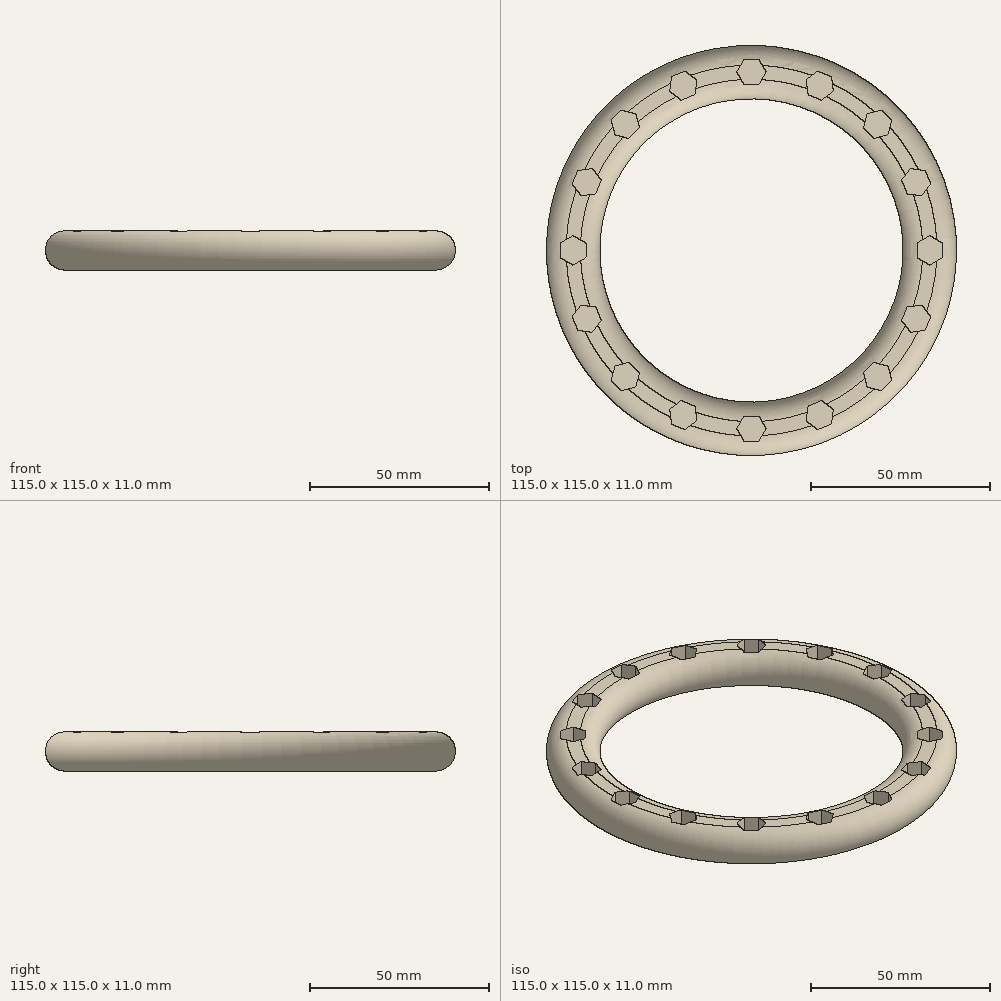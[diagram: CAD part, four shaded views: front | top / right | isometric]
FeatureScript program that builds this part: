
annotation { "Feature Type Name" : "Feature", "Feature Type Description" : "" }
export const myFeature = defineFeature(function(context is Context, id is Id, definition is map)
    precondition{}
    {
        {
            var Q0;
            Q0=qCreatedBy(makeId("Front.planeOp"),FACE);
            var sketch = newSketch(context, id + "F0", { "sketchPlane" : qUnion([Q0])});
            skLineSegment(sketch, "E0.bottom", {"start": v(42.5, 11) * mm, "end": v(57.5, 11) * mm});
            skLineSegment(sketch, "E0.top", {"start": v(42.5, 0) * mm, "end": v(57.5, 0) * mm});
            skLineSegment(sketch, "E0.left", {"start": v(42.5, 11) * mm, "end": v(42.5, 0) * mm});
            skLineSegment(sketch, "E0.right", {"start": v(57.5, 11) * mm, "end": v(57.5, 0) * mm});
            skLineSegment(sketch, "E1", {"start": v(0, 0) * mm, "end": v(0, 22.77) * mm});
            skSolve(sketch);
        }
        {
            var Q0;
            Q0 = qSketchRegion(id + "F0", true);
            var Q1;
            Q1=sQuery(id+"F0.wireOp",EDGE,"E1");
            revolve(context, id + "F1", {"entities" : qUnion([Q0]), "axis" : qUnion([Q1]), "revolveType" : RevolveType.FULL});
        }
        {
            var Q0;
            Q0=makeQuery(id+"F1.opRevolve","SWEPT_FACE",FACE,{"disambiguationData":[OSD([sQuery(id+"F0.wireOp",EDGE,"E0.bottom")])]});
            var sketch = newSketch(context, id + "F2", { "sketchPlane" : qUnion([Q0])});
            skCircle(sketch, "E2.cCircle", {"center": v(0, 50) * mm, "radius": 3.58 * mm, "construction": true});
            skLineSegment(sketch, "E2.0", {"start": v(2.06, 46.43) * mm, "end": v(-2.06, 46.43) * mm});
            skLineSegment(sketch, "E2.1", {"start": v(-2.06, 46.43) * mm, "end": v(-4.13, 50) * mm});
            skLineSegment(sketch, "E2.2", {"start": v(-4.13, 50) * mm, "end": v(-2.06, 53.58) * mm});
            skLineSegment(sketch, "E2.3", {"start": v(-2.06, 53.58) * mm, "end": v(2.06, 53.58) * mm});
            skLineSegment(sketch, "E2.4", {"start": v(2.06, 53.57) * mm, "end": v(4.13, 50) * mm});
            skLineSegment(sketch, "E2.5", {"start": v(4.13, 50) * mm, "end": v(2.06, 46.43) * mm});
            skPoint(sketch, "E2.0.midPoint", {"position": v(0, 46.43) * mm});
            skCircle(sketch, "E3.1.0", {"center": v(-19.13, 46.2) * mm, "radius": 3.58 * mm, "construction": true});
            skPoint(sketch, "E3.1.1", {"position": v(-17.77, 42.9) * mm});
            skLineSegment(sketch, "E3.1.2", {"start": v(-15.32, 47.77) * mm, "end": v(-15.86, 43.68) * mm});
            skLineSegment(sketch, "E3.1.3", {"start": v(-18.6, 50.29) * mm, "end": v(-15.32, 47.77) * mm});
            skLineSegment(sketch, "E3.1.4", {"start": v(-22.4, 48.7) * mm, "end": v(-18.6, 50.29) * mm});
            skLineSegment(sketch, "E3.1.5", {"start": v(-22.95, 44.61) * mm, "end": v(-22.4, 48.7) * mm});
            skLineSegment(sketch, "E3.1.6", {"start": v(-19.67, 42.1) * mm, "end": v(-22.95, 44.61) * mm});
            skLineSegment(sketch, "E3.1.7", {"start": v(-15.86, 43.68) * mm, "end": v(-19.67, 42.1) * mm});
            skCircle(sketch, "E3.2.0", {"center": v(-35.36, 35.36) * mm, "radius": 3.58 * mm, "construction": true});
            skPoint(sketch, "E3.2.1", {"position": v(-32.83, 32.83) * mm});
            skLineSegment(sketch, "E3.2.2", {"start": v(-32.44, 38.27) * mm, "end": v(-31.37, 34.29) * mm});
            skLineSegment(sketch, "E3.2.3", {"start": v(-36.42, 39.34) * mm, "end": v(-32.44, 38.27) * mm});
            skLineSegment(sketch, "E3.2.4", {"start": v(-39.34, 36.42) * mm, "end": v(-36.42, 39.34) * mm});
            skLineSegment(sketch, "E3.2.5", {"start": v(-38.27, 32.44) * mm, "end": v(-39.34, 36.42) * mm});
            skLineSegment(sketch, "E3.2.6", {"start": v(-34.29, 31.37) * mm, "end": v(-38.27, 32.44) * mm});
            skLineSegment(sketch, "E3.2.7", {"start": v(-31.37, 34.29) * mm, "end": v(-34.29, 31.37) * mm});
            skCircle(sketch, "E3.3.0", {"center": v(-46.2, 19.13) * mm, "radius": 3.58 * mm, "construction": true});
            skPoint(sketch, "E3.3.1", {"position": v(-42.9, 17.77) * mm});
            skLineSegment(sketch, "E3.3.2", {"start": v(-44.61, 22.95) * mm, "end": v(-42.1, 19.67) * mm});
            skLineSegment(sketch, "E3.3.3", {"start": v(-48.7, 22.4) * mm, "end": v(-44.61, 22.95) * mm});
            skLineSegment(sketch, "E3.3.4", {"start": v(-50.29, 18.6) * mm, "end": v(-48.7, 22.4) * mm});
            skLineSegment(sketch, "E3.3.5", {"start": v(-47.77, 15.32) * mm, "end": v(-50.29, 18.6) * mm});
            skLineSegment(sketch, "E3.3.6", {"start": v(-43.68, 15.86) * mm, "end": v(-47.77, 15.32) * mm});
            skLineSegment(sketch, "E3.3.7", {"start": v(-42.1, 19.67) * mm, "end": v(-43.68, 15.86) * mm});
            skCircle(sketch, "E3.4.0", {"center": v(-50, 0) * mm, "radius": 3.58 * mm, "construction": true});
            skPoint(sketch, "E3.4.1", {"position": v(-46.42, 0) * mm});
            skLineSegment(sketch, "E3.4.2", {"start": v(-50, 4.13) * mm, "end": v(-46.43, 2.06) * mm});
            skLineSegment(sketch, "E3.4.3", {"start": v(-53.57, 2.06) * mm, "end": v(-50, 4.13) * mm});
            skLineSegment(sketch, "E3.4.4", {"start": v(-53.57, -2.06) * mm, "end": v(-53.57, 2.06) * mm});
            skLineSegment(sketch, "E3.4.5", {"start": v(-50, -4.13) * mm, "end": v(-53.58, -2.06) * mm});
            skLineSegment(sketch, "E3.4.6", {"start": v(-46.43, -2.06) * mm, "end": v(-50, -4.13) * mm});
            skLineSegment(sketch, "E3.4.7", {"start": v(-46.42, 2.06) * mm, "end": v(-46.42, -2.06) * mm});
            skCircle(sketch, "E3.5.0", {"center": v(-46.2, -19.13) * mm, "radius": 3.58 * mm, "construction": true});
            skPoint(sketch, "E3.5.1", {"position": v(-42.9, -17.77) * mm});
            skLineSegment(sketch, "E3.5.2", {"start": v(-47.77, -15.32) * mm, "end": v(-43.68, -15.86) * mm});
            skLineSegment(sketch, "E3.5.3", {"start": v(-50.29, -18.6) * mm, "end": v(-47.77, -15.32) * mm});
            skLineSegment(sketch, "E3.5.4", {"start": v(-48.7, -22.4) * mm, "end": v(-50.29, -18.6) * mm});
            skLineSegment(sketch, "E3.5.5", {"start": v(-44.61, -22.95) * mm, "end": v(-48.7, -22.4) * mm});
            skLineSegment(sketch, "E3.5.6", {"start": v(-42.1, -19.67) * mm, "end": v(-44.61, -22.95) * mm});
            skLineSegment(sketch, "E3.5.7", {"start": v(-43.68, -15.86) * mm, "end": v(-42.1, -19.67) * mm});
            skCircle(sketch, "E3.6.0", {"center": v(-35.36, -35.36) * mm, "radius": 3.58 * mm, "construction": true});
            skPoint(sketch, "E3.6.1", {"position": v(-32.83, -32.83) * mm});
            skLineSegment(sketch, "E3.6.2", {"start": v(-38.27, -32.44) * mm, "end": v(-34.29, -31.37) * mm});
            skLineSegment(sketch, "E3.6.3", {"start": v(-39.34, -36.42) * mm, "end": v(-38.27, -32.44) * mm});
            skLineSegment(sketch, "E3.6.4", {"start": v(-36.42, -39.34) * mm, "end": v(-39.34, -36.42) * mm});
            skLineSegment(sketch, "E3.6.5", {"start": v(-32.44, -38.27) * mm, "end": v(-36.42, -39.34) * mm});
            skLineSegment(sketch, "E3.6.6", {"start": v(-31.37, -34.29) * mm, "end": v(-32.44, -38.27) * mm});
            skLineSegment(sketch, "E3.6.7", {"start": v(-34.29, -31.37) * mm, "end": v(-31.37, -34.29) * mm});
            skCircle(sketch, "E3.7.0", {"center": v(-19.13, -46.2) * mm, "radius": 3.58 * mm, "construction": true});
            skPoint(sketch, "E3.7.1", {"position": v(-17.77, -42.9) * mm});
            skLineSegment(sketch, "E3.7.2", {"start": v(-22.95, -44.61) * mm, "end": v(-19.67, -42.1) * mm});
            skLineSegment(sketch, "E3.7.3", {"start": v(-22.4, -48.7) * mm, "end": v(-22.95, -44.61) * mm});
            skLineSegment(sketch, "E3.7.4", {"start": v(-18.6, -50.29) * mm, "end": v(-22.4, -48.7) * mm});
            skLineSegment(sketch, "E3.7.5", {"start": v(-15.32, -47.77) * mm, "end": v(-18.6, -50.29) * mm});
            skLineSegment(sketch, "E3.7.6", {"start": v(-15.86, -43.68) * mm, "end": v(-15.32, -47.77) * mm});
            skLineSegment(sketch, "E3.7.7", {"start": v(-19.67, -42.1) * mm, "end": v(-15.86, -43.68) * mm});
            skCircle(sketch, "E3.8.0", {"center": v(0, -50) * mm, "radius": 3.58 * mm, "construction": true});
            skPoint(sketch, "E3.8.1", {"position": v(0, -46.43) * mm});
            skLineSegment(sketch, "E3.8.2", {"start": v(-4.13, -50) * mm, "end": v(-2.06, -46.43) * mm});
            skLineSegment(sketch, "E3.8.3", {"start": v(-2.06, -53.57) * mm, "end": v(-4.13, -50) * mm});
            skLineSegment(sketch, "E3.8.4", {"start": v(2.06, -53.58) * mm, "end": v(-2.06, -53.58) * mm});
            skLineSegment(sketch, "E3.8.5", {"start": v(4.13, -50) * mm, "end": v(2.06, -53.58) * mm});
            skLineSegment(sketch, "E3.8.6", {"start": v(2.06, -46.43) * mm, "end": v(4.13, -50) * mm});
            skLineSegment(sketch, "E3.8.7", {"start": v(-2.06, -46.43) * mm, "end": v(2.06, -46.43) * mm});
            skCircle(sketch, "E3.9.0", {"center": v(19.13, -46.2) * mm, "radius": 3.58 * mm, "construction": true});
            skPoint(sketch, "E3.9.1", {"position": v(17.77, -42.9) * mm});
            skLineSegment(sketch, "E3.9.2", {"start": v(15.32, -47.77) * mm, "end": v(15.86, -43.68) * mm});
            skLineSegment(sketch, "E3.9.3", {"start": v(18.6, -50.29) * mm, "end": v(15.32, -47.77) * mm});
            skLineSegment(sketch, "E3.9.4", {"start": v(22.4, -48.7) * mm, "end": v(18.6, -50.29) * mm});
            skLineSegment(sketch, "E3.9.5", {"start": v(22.95, -44.61) * mm, "end": v(22.4, -48.7) * mm});
            skLineSegment(sketch, "E3.9.6", {"start": v(19.67, -42.1) * mm, "end": v(22.95, -44.61) * mm});
            skLineSegment(sketch, "E3.9.7", {"start": v(15.86, -43.68) * mm, "end": v(19.67, -42.1) * mm});
            skCircle(sketch, "E3.10.0", {"center": v(35.36, -35.36) * mm, "radius": 3.58 * mm, "construction": true});
            skPoint(sketch, "E3.10.1", {"position": v(32.83, -32.83) * mm});
            skLineSegment(sketch, "E3.10.2", {"start": v(32.44, -38.27) * mm, "end": v(31.37, -34.29) * mm});
            skLineSegment(sketch, "E3.10.3", {"start": v(36.42, -39.34) * mm, "end": v(32.44, -38.27) * mm});
            skLineSegment(sketch, "E3.10.4", {"start": v(39.34, -36.42) * mm, "end": v(36.42, -39.34) * mm});
            skLineSegment(sketch, "E3.10.5", {"start": v(38.27, -32.44) * mm, "end": v(39.34, -36.42) * mm});
            skLineSegment(sketch, "E3.10.6", {"start": v(34.29, -31.37) * mm, "end": v(38.27, -32.44) * mm});
            skLineSegment(sketch, "E3.10.7", {"start": v(31.37, -34.29) * mm, "end": v(34.29, -31.37) * mm});
            skCircle(sketch, "E3.11.0", {"center": v(46.2, -19.13) * mm, "radius": 3.58 * mm, "construction": true});
            skPoint(sketch, "E3.11.1", {"position": v(42.9, -17.77) * mm});
            skLineSegment(sketch, "E3.11.2", {"start": v(44.61, -22.95) * mm, "end": v(42.1, -19.67) * mm});
            skLineSegment(sketch, "E3.11.3", {"start": v(48.7, -22.4) * mm, "end": v(44.61, -22.95) * mm});
            skLineSegment(sketch, "E3.11.4", {"start": v(50.29, -18.6) * mm, "end": v(48.7, -22.4) * mm});
            skLineSegment(sketch, "E3.11.5", {"start": v(47.77, -15.32) * mm, "end": v(50.29, -18.6) * mm});
            skLineSegment(sketch, "E3.11.6", {"start": v(43.68, -15.86) * mm, "end": v(47.77, -15.32) * mm});
            skLineSegment(sketch, "E3.11.7", {"start": v(42.1, -19.67) * mm, "end": v(43.68, -15.86) * mm});
            skPoint(sketch, "E3.center", {"position": v(0, 0) * mm});
            skPoint(sketch, "E4.2.12.0", {"position": v(46.43, 0) * mm});
            skLineSegment(sketch, "E4.3.12.0", {"start": v(50, -4.13) * mm, "end": v(46.43, -2.06) * mm});
            skLineSegment(sketch, "E4.6.12.0", {"start": v(53.57, -2.06) * mm, "end": v(50, -4.13) * mm});
            skLineSegment(sketch, "E4.9.12.0", {"start": v(53.58, 2.06) * mm, "end": v(53.58, -2.06) * mm});
            skLineSegment(sketch, "E4.12.12.0", {"start": v(50, 4.13) * mm, "end": v(53.58, 2.06) * mm});
            skLineSegment(sketch, "E4.15.12.0", {"start": v(46.43, 2.06) * mm, "end": v(50, 4.13) * mm});
            skCircle(sketch, "E4.16.12.0", {"center": v(50, 0) * mm, "radius": 3.58 * mm, "construction": true});
            skLineSegment(sketch, "E4.18.12.0", {"start": v(46.43, -2.06) * mm, "end": v(46.43, 2.06) * mm});
            skPoint(sketch, "E4.2.13.0", {"position": v(42.9, 17.77) * mm});
            skLineSegment(sketch, "E4.3.13.0", {"start": v(47.77, 15.32) * mm, "end": v(43.68, 15.86) * mm});
            skLineSegment(sketch, "E4.6.13.0", {"start": v(50.29, 18.6) * mm, "end": v(47.77, 15.32) * mm});
            skLineSegment(sketch, "E4.9.13.0", {"start": v(48.7, 22.4) * mm, "end": v(50.29, 18.6) * mm});
            skLineSegment(sketch, "E4.12.13.0", {"start": v(44.61, 22.95) * mm, "end": v(48.7, 22.4) * mm});
            skLineSegment(sketch, "E4.15.13.0", {"start": v(42.1, 19.67) * mm, "end": v(44.61, 22.95) * mm});
            skCircle(sketch, "E4.16.13.0", {"center": v(46.2, 19.13) * mm, "radius": 3.58 * mm, "construction": true});
            skLineSegment(sketch, "E4.18.13.0", {"start": v(43.68, 15.86) * mm, "end": v(42.1, 19.67) * mm});
            skPoint(sketch, "E4.2.14.0", {"position": v(32.83, 32.83) * mm});
            skLineSegment(sketch, "E4.3.14.0", {"start": v(38.27, 32.44) * mm, "end": v(34.29, 31.37) * mm});
            skLineSegment(sketch, "E4.6.14.0", {"start": v(39.34, 36.42) * mm, "end": v(38.27, 32.44) * mm});
            skLineSegment(sketch, "E4.9.14.0", {"start": v(36.42, 39.34) * mm, "end": v(39.34, 36.42) * mm});
            skLineSegment(sketch, "E4.12.14.0", {"start": v(32.44, 38.27) * mm, "end": v(36.42, 39.34) * mm});
            skLineSegment(sketch, "E4.15.14.0", {"start": v(31.37, 34.29) * mm, "end": v(32.44, 38.27) * mm});
            skCircle(sketch, "E4.16.14.0", {"center": v(35.36, 35.36) * mm, "radius": 3.58 * mm, "construction": true});
            skLineSegment(sketch, "E4.18.14.0", {"start": v(34.29, 31.37) * mm, "end": v(31.37, 34.29) * mm});
            skPoint(sketch, "E4.2.15.0", {"position": v(17.77, 42.9) * mm});
            skLineSegment(sketch, "E4.3.15.0", {"start": v(22.95, 44.61) * mm, "end": v(19.67, 42.1) * mm});
            skLineSegment(sketch, "E4.6.15.0", {"start": v(22.4, 48.7) * mm, "end": v(22.95, 44.61) * mm});
            skLineSegment(sketch, "E4.9.15.0", {"start": v(18.6, 50.29) * mm, "end": v(22.4, 48.7) * mm});
            skLineSegment(sketch, "E4.12.15.0", {"start": v(15.32, 47.77) * mm, "end": v(18.6, 50.29) * mm});
            skLineSegment(sketch, "E4.15.15.0", {"start": v(15.86, 43.68) * mm, "end": v(15.32, 47.77) * mm});
            skCircle(sketch, "E4.16.15.0", {"center": v(19.13, 46.2) * mm, "radius": 3.58 * mm, "construction": true});
            skLineSegment(sketch, "E4.18.15.0", {"start": v(19.67, 42.1) * mm, "end": v(15.86, 43.68) * mm});
            skSolve(sketch);
        }
        {
            var Q0;
            Q0 = qSketchRegion(id + "F2", true);
            extrude(context, id + "F3", {"entities" : qUnion([Q0]), "operationType" : NewBodyOperationType.REMOVE, "oppositeDirection" : true, "depth" : 8.5 * mm});
        }
        {
            var Q0;
            Q0=makeQuery(id+"F1.opRevolve","SWEPT_EDGE",EDGE,{"disambiguationData":[OSD([sQuery(id+"F0.wireOp",EDGE,"E0.bottom"),sQuery(id+"F0.wireOp",EDGE,"E0.left")])]});
            var Q1;
            Q1=makeQuery(id+"F1.opRevolve","SWEPT_EDGE",EDGE,{"disambiguationData":[OSD([sQuery(id+"F0.wireOp",EDGE,"E0.bottom"),sQuery(id+"F0.wireOp",EDGE,"E0.right")])]});
            var Q2;
            Q2=makeQuery(id+"F1.opRevolve","SWEPT_EDGE",EDGE,{"disambiguationData":[OSD([sQuery(id+"F0.wireOp",EDGE,"E0.top"),sQuery(id+"F0.wireOp",EDGE,"E0.right")])]});
            var Q3;
            Q3=makeQuery(id+"F1.opRevolve","SWEPT_EDGE",EDGE,{"disambiguationData":[OSD([sQuery(id+"F0.wireOp",EDGE,"E0.top"),sQuery(id+"F0.wireOp",EDGE,"E0.left")])]});
            fillet(context, id + "F4", {"entities" : qUnion([Q0, Q1, Q2, Q3]), "radius" : 5.5 * mm, "tangentPropagation" : true, "allowEdgeOverflow" : false});
        }
    });
